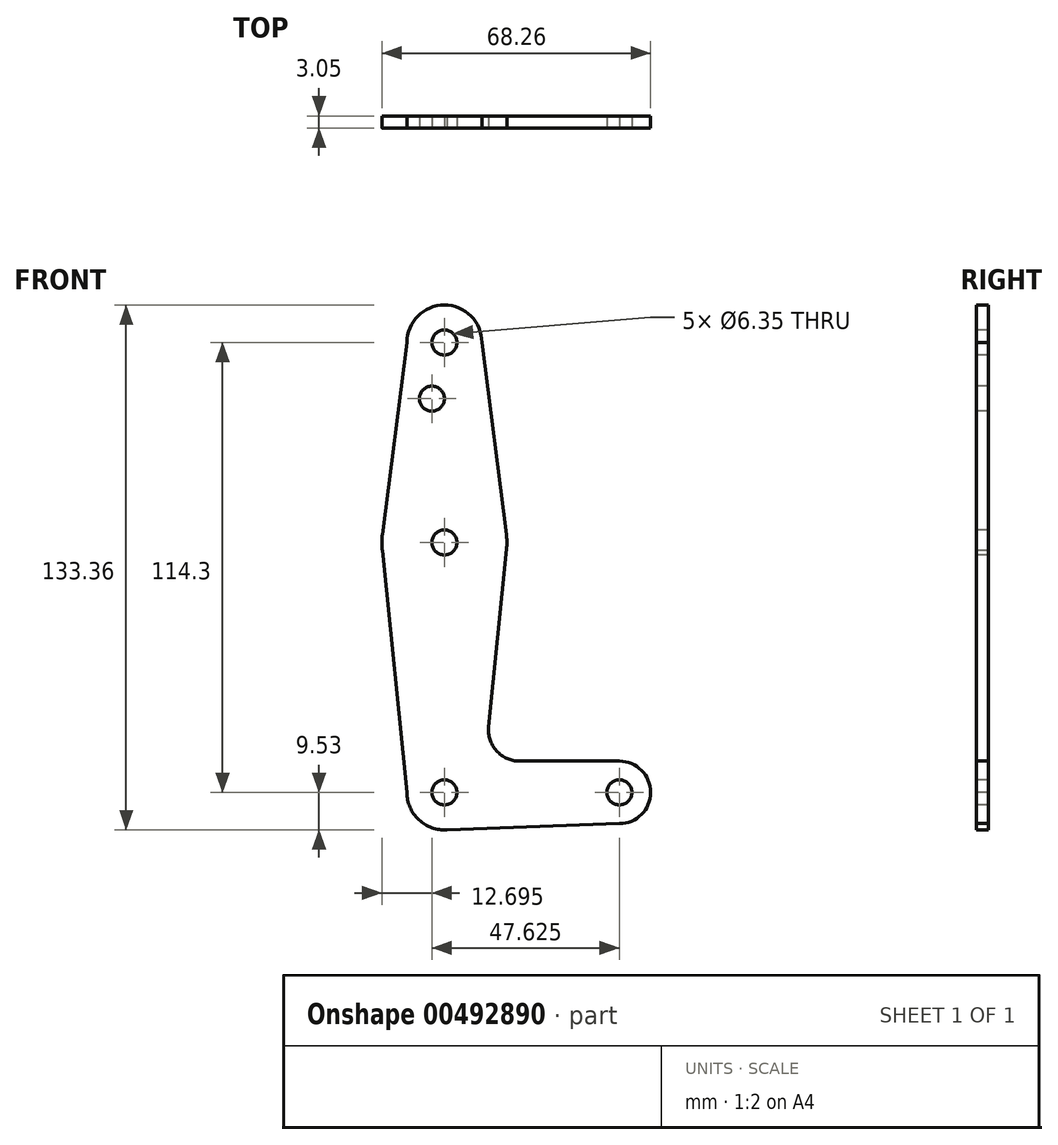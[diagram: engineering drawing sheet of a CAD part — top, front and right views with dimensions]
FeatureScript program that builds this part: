
annotation { "Feature Type Name" : "Feature", "Feature Type Description" : "" }
export const myFeature = defineFeature(function(context is Context, id is Id, definition is map)
    precondition{}
    {
        {
            var Q0;
            Q0=qCreatedBy(makeId("Front.planeOp"),FACE);
            var sketch = newSketch(context, id + "F0", { "sketchPlane" : qUnion([Q0])});
            skLineSegment(sketch, "E0", {"start": v(0, 0) * mm, "end": v(0, 114.3) * mm, "construction": true});
            skLineSegment(sketch, "E1", {"start": v(0, 0) * mm, "end": v(44.45, 0) * mm, "construction": true});
            skCircle(sketch, "E2", {"center": v(0, 114.3) * mm, "radius": 9.53 * mm});
            skCircle(sketch, "E3", {"center": v(0, 63.5) * mm, "radius": 15.88 * mm});
            skCircle(sketch, "E4", {"center": v(0, 0) * mm, "radius": 9.53 * mm});
            skCircle(sketch, "E5", {"center": v(44.45, 0) * mm, "radius": 7.94 * mm});
            skLineSegment(sketch, "E6", {"start": v(-9.53, 114.3) * mm, "end": v(-15.75, 65.5) * mm});
            skLineSegment(sketch, "E7", {"start": v(9.53, 114.3) * mm, "end": v(15.75, 65.5) * mm});
            skLineSegment(sketch, "E8", {"start": v(-9.53, 0) * mm, "end": v(-15.75, 61.5) * mm});
            skLineSegment(sketch, "E9", {"start": v(11.22, 16.69) * mm, "end": v(15.8, 61.9) * mm});
            skLineSegment(sketch, "E10", {"start": v(19.12, 7.94) * mm, "end": v(44.45, 7.94) * mm});
            skLineSegment(sketch, "E11", {"start": v(0, -9.52) * mm, "end": v(44.45, -7.94) * mm});
            skCircle(sketch, "E12", {"center": v(0, 114.3) * mm, "radius": 3.18 * mm});
            skCircle(sketch, "E13", {"center": v(0, 63.5) * mm, "radius": 3.18 * mm});
            skCircle(sketch, "E14", {"center": v(0, 0) * mm, "radius": 3.18 * mm});
            skCircle(sketch, "E15", {"center": v(44.45, 0) * mm, "radius": 3.18 * mm});
            skCircle(sketch, "E16", {"center": v(-3.18, 100.03) * mm, "radius": 3.17 * mm});
            skArc(sketch, "E17.filletArc", {"start": v(11.22, 16.69) * mm, "mid": v(13.23, 10.56) * mm, "end": v(19.12, 7.94) * mm});
            skSolve(sketch);
        }
        {
            var Q0;
            Q0 = qSketchRegion(id + "F0", true);
            extrude(context, id + "F1", {"entities" : qUnion([Q0]), "oppositeDirection" : true, "depth" : 3.05 * mm});
        }
    });
